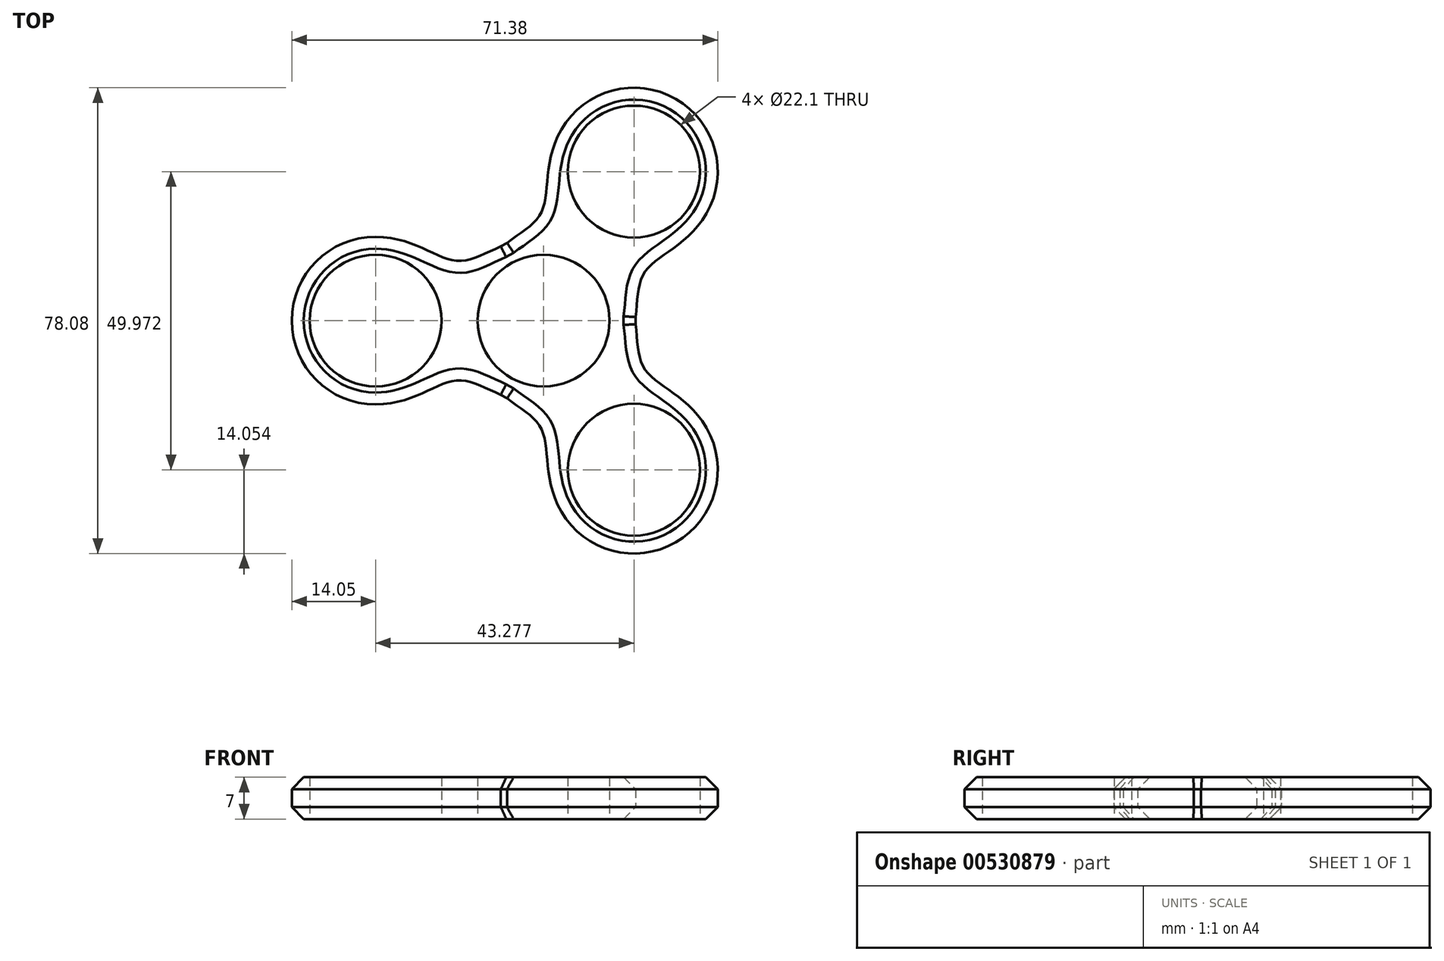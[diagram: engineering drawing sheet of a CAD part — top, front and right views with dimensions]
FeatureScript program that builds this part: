
annotation { "Feature Type Name" : "Feature", "Feature Type Description" : "" }
export const myFeature = defineFeature(function(context is Context, id is Id, definition is map)
    precondition{}
    {
        {
            var Q0;
            Q0=qCreatedBy(makeId("Top.planeOp"),FACE);
            var sketch = newSketch(context, id + "F0", { "sketchPlane" : qUnion([Q0])});
            skCircle(sketch, "E0", {"center": v(0, 0) * mm, "radius": 11 * mm, "construction": true});
            skCircle(sketch, "E1.0", {"center": v(0, 0) * mm, "radius": 11.05 * mm});
            skLineSegment(sketch, "E2", {"start": v(-11.05, 0) * mm, "end": v(-28.15, 0) * mm, "construction": true});
            skCircle(sketch, "E3", {"center": v(-28.15, 0) * mm, "radius": 11 * mm, "construction": true});
            skCircle(sketch, "E4.0", {"center": v(-28.15, 0) * mm, "radius": 11.05 * mm});
            skCircle(sketch, "E5.0", {"center": v(0, 0) * mm, "radius": 14.05 * mm});
            skCircle(sketch, "E6.0", {"center": v(-28.15, 0) * mm, "radius": 14.05 * mm});
            skLineSegment(sketch, "E7", {"start": v(-11.05, 0) * mm, "end": v(-17.1, 0) * mm, "construction": true});
            skLineSegment(sketch, "E8", {"start": v(-14.08, 10) * mm, "end": v(-14.08, -10) * mm, "construction": true});
            skPoint(sketch, "E9", {"position": v(-14.08, 0) * mm});
            skLineSegment(sketch, "E10", {"start": v(-21.57, -10) * mm, "end": v(-6.58, -10) * mm, "construction": true});
            skPoint(sketch, "E11", {"position": v(-14.08, -10) * mm});
            skLineSegment(sketch, "E12.MirrorCS", {"start": v(-21.57, 10) * mm, "end": v(-6.58, 10) * mm, "construction": true});
            skLineSegment(sketch, "E13", {"start": v(-28.15, 0) * mm, "end": v(-28.15, -14.05) * mm, "construction": true});
            skLineSegment(sketch, "E14", {"start": v(0, 0) * mm, "end": v(0, -14.05) * mm, "construction": true});
            skLineSegment(sketch, "E15", {"start": v(-21.57, -10) * mm, "end": v(-21.57, -14.05) * mm, "construction": true});
            skLineSegment(sketch, "E16", {"start": v(-6.58, -10) * mm, "end": v(-6.58, -14.05) * mm, "construction": true});
            skFitSpline(sketch, "E17", {"points": [v(-28.15, -14.05) * mm, v(-14.08, -10) * mm, v(0, -14.05) * mm], "startDerivative": vector(39.45, 0) * mm, "endDerivative": vector(39.45, 0) * mm});
            skFitSpline(sketch, "E18.MirrorCS", {"points": [v(-28.15, 14.05) * mm, v(-14.08, 10) * mm, v(0, 14.05) * mm], "startDerivative": vector(39.45, 0) * mm, "endDerivative": vector(39.45, 0) * mm});
            skLineSegment(sketch, "E19.MirrorCS", {"start": v(-21.57, 10) * mm, "end": v(-21.57, 14.05) * mm, "construction": true});
            skLineSegment(sketch, "E20.MirrorCS", {"start": v(-6.58, 10) * mm, "end": v(-6.58, 14.05) * mm, "construction": true});
            skLineSegment(sketch, "E21.1.0", {"start": v(1.05, -0.6) * mm, "end": v(13.22, 6.42) * mm, "construction": true});
            skLineSegment(sketch, "E21.1.1", {"start": v(13, -1.3) * mm, "end": v(16.5, 0.72) * mm, "construction": true});
            skLineSegment(sketch, "E21.1.2", {"start": v(20.5, -14.3) * mm, "end": v(13, -1.3) * mm, "construction": true});
            skLineSegment(sketch, "E21.1.3", {"start": v(20.5, -14.3) * mm, "end": v(24, -12.27) * mm, "construction": true});
            skCircle(sketch, "E21.1.4", {"center": v(15.13, -24.99) * mm, "radius": 11.05 * mm});
            skLineSegment(sketch, "E21.1.5", {"start": v(15.13, -24.99) * mm, "end": v(27.3, -17.96) * mm, "construction": true});
            skLineSegment(sketch, "E21.1.6", {"start": v(6.58, -10.18) * mm, "end": v(9.6, -15.42) * mm, "construction": true});
            skCircle(sketch, "E21.1.7", {"center": v(15.13, -24.99) * mm, "radius": 14.05 * mm});
            skLineSegment(sketch, "E21.2.0", {"start": v(1.05, 0.6) * mm, "end": v(-11.12, 7.63) * mm, "construction": true});
            skLineSegment(sketch, "E21.2.1", {"start": v(-4.32, 11.3) * mm, "end": v(-7.83, 13.33) * mm, "construction": true});
            skLineSegment(sketch, "E21.2.2", {"start": v(3.18, 24.3) * mm, "end": v(-4.32, 11.3) * mm, "construction": true});
            skLineSegment(sketch, "E21.2.3", {"start": v(3.18, 24.3) * mm, "end": v(-0.33, 26.32) * mm, "construction": true});
            skCircle(sketch, "E21.2.4", {"center": v(15.13, 24.99) * mm, "radius": 11.05 * mm});
            skLineSegment(sketch, "E21.2.5", {"start": v(15.13, 24.99) * mm, "end": v(2.96, 32.01) * mm, "construction": true});
            skLineSegment(sketch, "E21.2.6", {"start": v(6.58, 10.18) * mm, "end": v(9.6, 15.42) * mm, "construction": true});
            skCircle(sketch, "E21.2.7", {"center": v(15.13, 24.99) * mm, "radius": 14.05 * mm});
            skPoint(sketch, "E21.center", {"position": v(0.7, 0) * mm});
            skFitSpline(sketch, "E22", {"points": [v(-11.12, 7.63) * mm, v(-0.57, 17.8) * mm, v(2.96, 32.01) * mm], "startDerivative": vector(19.73, 34.16) * mm, "endDerivative": vector(19.72, 34.16) * mm});
            skFitSpline(sketch, "E23.MirrorCS", {"points": [v(13.22, -6.42) * mm, v(16.75, 7.8) * mm, v(27.3, 17.96) * mm], "startDerivative": vector(19.72, 34.16) * mm, "endDerivative": vector(19.73, 34.16) * mm});
            skFitSpline(sketch, "E24", {"points": [v(13.22, 6.42) * mm, v(16.75, -7.8) * mm, v(27.3, -17.96) * mm], "startDerivative": vector(19.72, -34.16) * mm, "endDerivative": vector(19.73, -34.16) * mm});
            skFitSpline(sketch, "E25.MirrorCS", {"points": [v(-11.12, -7.63) * mm, v(-0.57, -17.8) * mm, v(2.96, -32.01) * mm], "startDerivative": vector(19.73, -34.16) * mm, "endDerivative": vector(19.72, -34.16) * mm});
            skSolve(sketch);
        }
        {
            var Q0;
            {var subQ3=sQuery(id+"F0.wireOp",EDGE,"E22");var subQ9=sQuery(id+"F0.wireOp",EDGE,"E5.0");var subQ10=makeQuery(id+"F0.imprint","INTERSECT",VERTEX,{"derivedFrom":[subQ9,subQ3]});Q0=makeQuery(id+"F0.imprint","IMPRINT",FACE,{"disambiguationData":[TD([[makeQuery(id+"F0.imprint","IMPRINT",EDGE,{"disambiguationData":[TD([[subQ10,-1.0]])],"derivedFrom":subQ9}),-1.0]])]});}
            var Q1;
            Q1=makeQuery(id+"F0.imprint","IMPRINT",FACE,{"disambiguationData":[TD([[makeQuery(id+"F0.imprint","IMPRINT",EDGE,{"derivedFrom":sQuery(id+"F0.wireOp",EDGE,"E1.0")}),-1.0]])]});
            var Q2;
            Q2=makeQuery(id+"F0.imprint","IMPRINT",FACE,{"disambiguationData":[TD([[makeQuery(id+"F0.imprint","IMPRINT",EDGE,{"derivedFrom":sQuery(id+"F0.wireOp",EDGE,"E4.0")}),-1.0]])]});
            var Q3;
            {var subQ1=sQuery(id+"F0.wireOp",EDGE,"E5.0");var subQ5=sQuery(id+"F0.wireOp",EDGE,"E17");var subQ6=makeQuery(id+"F0.imprint","INTERSECT",VERTEX,{"derivedFrom":[subQ1,subQ5]});Q3=makeQuery(id+"F0.imprint","IMPRINT",FACE,{"disambiguationData":[TD([[makeQuery(id+"F0.imprint","IMPRINT",EDGE,{"disambiguationData":[TD([[subQ6,-1.0]])],"derivedFrom":subQ1}),-1.0]])]});}
            var Q4;
            Q4=makeQuery(id+"F0.imprint","IMPRINT",FACE,{"disambiguationData":[TD([[makeQuery(id+"F0.imprint","IMPRINT",EDGE,{"derivedFrom":sQuery(id+"F0.wireOp",EDGE,"E21.1.4")}),-1.0]])]});
            var Q5;
            {var subQ3=sQuery(id+"F0.wireOp",EDGE,"E18.MirrorCS");var subQ7=sQuery(id+"F0.wireOp",EDGE,"E5.0");var subQ8=makeQuery(id+"F0.imprint","INTERSECT",VERTEX,{"derivedFrom":[subQ7,subQ3]});Q5=makeQuery(id+"F0.imprint","IMPRINT",FACE,{"disambiguationData":[TD([[makeQuery(id+"F0.imprint","IMPRINT",EDGE,{"disambiguationData":[TD([[subQ8,1.0]])],"derivedFrom":subQ7}),-1.0]])]});}
            var Q6;
            Q6=makeQuery(id+"F0.imprint","IMPRINT",FACE,{"disambiguationData":[TD([[makeQuery(id+"F0.imprint","IMPRINT",EDGE,{"derivedFrom":sQuery(id+"F0.wireOp",EDGE,"E21.2.4")}),-1.0]])]});
            var Q7;
            {var subQ0=sQuery(id+"F0.wireOp",EDGE,"E18.MirrorCS");var subQ1=sQuery(id+"F0.wireOp",EDGE,"E5.0");var subQ2=makeQuery(id+"F0.imprint","INTERSECT",VERTEX,{"derivedFrom":[subQ1,subQ0]});Q7=makeQuery(id+"F0.imprint","IMPRINT",FACE,{"disambiguationData":[TD([[makeQuery(id+"F0.imprint","IMPRINT",EDGE,{"disambiguationData":[TD([[subQ2,-1.0]])],"derivedFrom":subQ1}),-1.0]])]});}
            var Q8;
            {var subQ0=sQuery(id+"F0.wireOp",EDGE,"E17");var subQ1=sQuery(id+"F0.wireOp",EDGE,"E5.0");var subQ2=makeQuery(id+"F0.imprint","INTERSECT",VERTEX,{"derivedFrom":[subQ1,subQ0]});Q8=makeQuery(id+"F0.imprint","IMPRINT",FACE,{"disambiguationData":[TD([[makeQuery(id+"F0.imprint","IMPRINT",EDGE,{"disambiguationData":[TD([[subQ2,1.0]])],"derivedFrom":subQ1}),-1.0]])]});}
            var Q9;
            {var subQ0=sQuery(id+"F0.wireOp",EDGE,"E23.MirrorCS");var subQ1=sQuery(id+"F0.wireOp",EDGE,"E5.0");var subQ2=makeQuery(id+"F0.imprint","INTERSECT",VERTEX,{"derivedFrom":[subQ1,subQ0]});Q9=makeQuery(id+"F0.imprint","IMPRINT",FACE,{"disambiguationData":[TD([[makeQuery(id+"F0.imprint","IMPRINT",EDGE,{"disambiguationData":[TD([[subQ2,-1.0]])],"derivedFrom":subQ1}),-1.0]])]});}
            extrude(context, id + "F1", {"entities" : qUnion([Q0, Q1, Q2, Q3, Q4, Q5, Q6, Q7, Q8, Q9]), "depth" : 7 * mm, "offsetDistance" : 25 * mm});
        }
        {
            var Q0;
            Q0=makeQuery(id+"F1.opExtrude","SWEPT_EDGE",EDGE,{"disambiguationData":[OSD([sQuery(id+"F0.wireOp",EDGE,"E17"),sQuery(id+"F0.wireOp",EDGE,"E25.MirrorCS")])]});
            var Q1;
            Q1=makeQuery(id+"F1.opExtrude","SWEPT_EDGE",EDGE,{"disambiguationData":[OSD([sQuery(id+"F0.wireOp",EDGE,"E23.MirrorCS"),sQuery(id+"F0.wireOp",EDGE,"E24")])]});
            var Q2;
            Q2=makeQuery(id+"F1.opExtrude","SWEPT_EDGE",EDGE,{"disambiguationData":[OSD([sQuery(id+"F0.wireOp",EDGE,"E18.MirrorCS"),sQuery(id+"F0.wireOp",EDGE,"E22")])]});
            chamfer(context, id + "F2", {"entities" : qUnion([Q0, Q1, Q2]), "width" : 5 * mm, "tangentPropagation" : true});
        }
        {
            var Q0;
            Q0=makeQuery(id+"F1.opExtrude","CAP_EDGE",EDGE,{"disambiguationData":[OSD([sQuery(id+"F0.wireOp",EDGE,"E21.1.7")])],"isStart":false});
            var Q1;
            Q1=makeQuery(id+"F1.opExtrude","CAP_EDGE",EDGE,{"disambiguationData":[OSD([sQuery(id+"F0.wireOp",EDGE,"E21.2.7")])],"isStart":true});
            var Q2;
            Q2=makeQuery(id+"F1.opExtrude","CAP_EDGE",EDGE,{"disambiguationData":[OSD([sQuery(id+"F0.wireOp",EDGE,"E6.0")])],"isStart":true});
            var Q3;
            Q3=makeQuery(id+"F1.opExtrude","CAP_EDGE",EDGE,{"disambiguationData":[OSD([sQuery(id+"F0.wireOp",EDGE,"E21.1.7")])],"isStart":true});
            var Q4;
            {var subQ0=sQuery(id+"F0.wireOp",EDGE,"E24");var subQ1=sQuery(id+"F0.wireOp",EDGE,"E23.MirrorCS");Q4=makeQuery(id+"F2.opChamfer","BLEND_EDGE",EDGE,{"blendedFrom":[makeQuery(id+"F1.opExtrude","SWEPT_EDGE",EDGE,{"disambiguationData":[OSD([subQ1,subQ0])]}),makeQuery(id+"F1.opExtrude","CAP_FACE",FACE,{"disambiguationData":[OSD([sQuery(id+"F0.wireOp",EDGE,"E1.0"),sQuery(id+"F0.wireOp",EDGE,"E4.0"),sQuery(id+"F0.wireOp",EDGE,"E6.0"),sQuery(id+"F0.wireOp",EDGE,"E17"),sQuery(id+"F0.wireOp",EDGE,"E18.MirrorCS"),sQuery(id+"F0.wireOp",EDGE,"E21.1.4"),sQuery(id+"F0.wireOp",EDGE,"E21.1.7"),sQuery(id+"F0.wireOp",EDGE,"E21.2.4"),sQuery(id+"F0.wireOp",EDGE,"E21.2.7"),sQuery(id+"F0.wireOp",EDGE,"E22"),subQ1,subQ0,sQuery(id+"F0.wireOp",EDGE,"E25.MirrorCS")])],"isStart":false})],"blendedInto":[makeQuery(id+"F1.opExtrude","CAP_FACE",FACE,{"disambiguationData":[OSD([sQuery(id+"F0.wireOp",EDGE,"E1.0"),sQuery(id+"F0.wireOp",EDGE,"E4.0"),sQuery(id+"F0.wireOp",EDGE,"E6.0"),sQuery(id+"F0.wireOp",EDGE,"E17"),sQuery(id+"F0.wireOp",EDGE,"E18.MirrorCS"),sQuery(id+"F0.wireOp",EDGE,"E21.1.4"),sQuery(id+"F0.wireOp",EDGE,"E21.1.7"),sQuery(id+"F0.wireOp",EDGE,"E21.2.4"),sQuery(id+"F0.wireOp",EDGE,"E21.2.7"),sQuery(id+"F0.wireOp",EDGE,"E22"),subQ1,subQ0,sQuery(id+"F0.wireOp",EDGE,"E25.MirrorCS")])],"isStart":false})]});}
            var Q5;
            Q5=makeQuery(id+"F1.opExtrude","SWEPT_FACE",FACE,{"disambiguationData":[OSD([sQuery(id+"F0.wireOp",EDGE,"E6.0")])]});
            var Q6;
            {var subQ0=sQuery(id+"F0.wireOp",EDGE,"E22");var subQ1=sQuery(id+"F0.wireOp",EDGE,"E18.MirrorCS");Q6=makeQuery(id+"F2.opChamfer","BLEND_EDGE",EDGE,{"blendedFrom":[makeQuery(id+"F1.opExtrude","SWEPT_EDGE",EDGE,{"disambiguationData":[OSD([subQ1,subQ0])]}),makeQuery(id+"F1.opExtrude","CAP_FACE",FACE,{"disambiguationData":[OSD([sQuery(id+"F0.wireOp",EDGE,"E1.0"),sQuery(id+"F0.wireOp",EDGE,"E4.0"),sQuery(id+"F0.wireOp",EDGE,"E6.0"),sQuery(id+"F0.wireOp",EDGE,"E17"),subQ1,sQuery(id+"F0.wireOp",EDGE,"E21.1.4"),sQuery(id+"F0.wireOp",EDGE,"E21.1.7"),sQuery(id+"F0.wireOp",EDGE,"E21.2.4"),sQuery(id+"F0.wireOp",EDGE,"E21.2.7"),subQ0,sQuery(id+"F0.wireOp",EDGE,"E23.MirrorCS"),sQuery(id+"F0.wireOp",EDGE,"E24"),sQuery(id+"F0.wireOp",EDGE,"E25.MirrorCS")])],"isStart":false})],"blendedInto":[makeQuery(id+"F1.opExtrude","CAP_FACE",FACE,{"disambiguationData":[OSD([sQuery(id+"F0.wireOp",EDGE,"E1.0"),sQuery(id+"F0.wireOp",EDGE,"E4.0"),sQuery(id+"F0.wireOp",EDGE,"E6.0"),sQuery(id+"F0.wireOp",EDGE,"E17"),subQ1,sQuery(id+"F0.wireOp",EDGE,"E21.1.4"),sQuery(id+"F0.wireOp",EDGE,"E21.1.7"),sQuery(id+"F0.wireOp",EDGE,"E21.2.4"),sQuery(id+"F0.wireOp",EDGE,"E21.2.7"),subQ0,sQuery(id+"F0.wireOp",EDGE,"E23.MirrorCS"),sQuery(id+"F0.wireOp",EDGE,"E24"),sQuery(id+"F0.wireOp",EDGE,"E25.MirrorCS")])],"isStart":false})]});}
            var Q7;
            Q7=makeQuery(id+"F1.opExtrude","CAP_EDGE",EDGE,{"disambiguationData":[OSD([sQuery(id+"F0.wireOp",EDGE,"E21.2.7")])],"isStart":false});
            var Q8;
            {var subQ0=sQuery(id+"F0.wireOp",EDGE,"E25.MirrorCS");var subQ1=sQuery(id+"F0.wireOp",EDGE,"E17");Q8=makeQuery(id+"F2.opChamfer","BLEND_EDGE",EDGE,{"blendedFrom":[makeQuery(id+"F1.opExtrude","SWEPT_EDGE",EDGE,{"disambiguationData":[OSD([subQ1,subQ0])]}),makeQuery(id+"F1.opExtrude","CAP_FACE",FACE,{"disambiguationData":[OSD([sQuery(id+"F0.wireOp",EDGE,"E1.0"),sQuery(id+"F0.wireOp",EDGE,"E4.0"),sQuery(id+"F0.wireOp",EDGE,"E6.0"),subQ1,sQuery(id+"F0.wireOp",EDGE,"E18.MirrorCS"),sQuery(id+"F0.wireOp",EDGE,"E21.1.4"),sQuery(id+"F0.wireOp",EDGE,"E21.1.7"),sQuery(id+"F0.wireOp",EDGE,"E21.2.4"),sQuery(id+"F0.wireOp",EDGE,"E21.2.7"),sQuery(id+"F0.wireOp",EDGE,"E22"),sQuery(id+"F0.wireOp",EDGE,"E23.MirrorCS"),sQuery(id+"F0.wireOp",EDGE,"E24"),subQ0])],"isStart":false})],"blendedInto":[makeQuery(id+"F1.opExtrude","CAP_FACE",FACE,{"disambiguationData":[OSD([sQuery(id+"F0.wireOp",EDGE,"E1.0"),sQuery(id+"F0.wireOp",EDGE,"E4.0"),sQuery(id+"F0.wireOp",EDGE,"E6.0"),subQ1,sQuery(id+"F0.wireOp",EDGE,"E18.MirrorCS"),sQuery(id+"F0.wireOp",EDGE,"E21.1.4"),sQuery(id+"F0.wireOp",EDGE,"E21.1.7"),sQuery(id+"F0.wireOp",EDGE,"E21.2.4"),sQuery(id+"F0.wireOp",EDGE,"E21.2.7"),sQuery(id+"F0.wireOp",EDGE,"E22"),sQuery(id+"F0.wireOp",EDGE,"E23.MirrorCS"),sQuery(id+"F0.wireOp",EDGE,"E24"),subQ0])],"isStart":false})]});}
            var Q9;
            {var subQ0=sQuery(id+"F0.wireOp",EDGE,"E25.MirrorCS");var subQ1=sQuery(id+"F0.wireOp",EDGE,"E17");Q9=makeQuery(id+"F2.opChamfer","BLEND_EDGE",EDGE,{"blendedFrom":[makeQuery(id+"F1.opExtrude","SWEPT_EDGE",EDGE,{"disambiguationData":[OSD([subQ1,subQ0])]}),makeQuery(id+"F1.opExtrude","CAP_FACE",FACE,{"disambiguationData":[OSD([sQuery(id+"F0.wireOp",EDGE,"E1.0"),sQuery(id+"F0.wireOp",EDGE,"E4.0"),sQuery(id+"F0.wireOp",EDGE,"E6.0"),subQ1,sQuery(id+"F0.wireOp",EDGE,"E18.MirrorCS"),sQuery(id+"F0.wireOp",EDGE,"E21.1.4"),sQuery(id+"F0.wireOp",EDGE,"E21.1.7"),sQuery(id+"F0.wireOp",EDGE,"E21.2.4"),sQuery(id+"F0.wireOp",EDGE,"E21.2.7"),sQuery(id+"F0.wireOp",EDGE,"E22"),sQuery(id+"F0.wireOp",EDGE,"E23.MirrorCS"),sQuery(id+"F0.wireOp",EDGE,"E24"),subQ0])],"isStart":true})],"blendedInto":[makeQuery(id+"F1.opExtrude","CAP_FACE",FACE,{"disambiguationData":[OSD([sQuery(id+"F0.wireOp",EDGE,"E1.0"),sQuery(id+"F0.wireOp",EDGE,"E4.0"),sQuery(id+"F0.wireOp",EDGE,"E6.0"),subQ1,sQuery(id+"F0.wireOp",EDGE,"E18.MirrorCS"),sQuery(id+"F0.wireOp",EDGE,"E21.1.4"),sQuery(id+"F0.wireOp",EDGE,"E21.1.7"),sQuery(id+"F0.wireOp",EDGE,"E21.2.4"),sQuery(id+"F0.wireOp",EDGE,"E21.2.7"),sQuery(id+"F0.wireOp",EDGE,"E22"),sQuery(id+"F0.wireOp",EDGE,"E23.MirrorCS"),sQuery(id+"F0.wireOp",EDGE,"E24"),subQ0])],"isStart":true})]});}
            var Q10;
            {var subQ0=sQuery(id+"F0.wireOp",EDGE,"E24");var subQ1=sQuery(id+"F0.wireOp",EDGE,"E23.MirrorCS");Q10=makeQuery(id+"F2.opChamfer","BLEND_EDGE",EDGE,{"blendedFrom":[makeQuery(id+"F1.opExtrude","SWEPT_EDGE",EDGE,{"disambiguationData":[OSD([subQ1,subQ0])]}),makeQuery(id+"F1.opExtrude","CAP_FACE",FACE,{"disambiguationData":[OSD([sQuery(id+"F0.wireOp",EDGE,"E1.0"),sQuery(id+"F0.wireOp",EDGE,"E4.0"),sQuery(id+"F0.wireOp",EDGE,"E6.0"),sQuery(id+"F0.wireOp",EDGE,"E17"),sQuery(id+"F0.wireOp",EDGE,"E18.MirrorCS"),sQuery(id+"F0.wireOp",EDGE,"E21.1.4"),sQuery(id+"F0.wireOp",EDGE,"E21.1.7"),sQuery(id+"F0.wireOp",EDGE,"E21.2.4"),sQuery(id+"F0.wireOp",EDGE,"E21.2.7"),sQuery(id+"F0.wireOp",EDGE,"E22"),subQ1,subQ0,sQuery(id+"F0.wireOp",EDGE,"E25.MirrorCS")])],"isStart":true})],"blendedInto":[makeQuery(id+"F1.opExtrude","CAP_FACE",FACE,{"disambiguationData":[OSD([sQuery(id+"F0.wireOp",EDGE,"E1.0"),sQuery(id+"F0.wireOp",EDGE,"E4.0"),sQuery(id+"F0.wireOp",EDGE,"E6.0"),sQuery(id+"F0.wireOp",EDGE,"E17"),sQuery(id+"F0.wireOp",EDGE,"E18.MirrorCS"),sQuery(id+"F0.wireOp",EDGE,"E21.1.4"),sQuery(id+"F0.wireOp",EDGE,"E21.1.7"),sQuery(id+"F0.wireOp",EDGE,"E21.2.4"),sQuery(id+"F0.wireOp",EDGE,"E21.2.7"),sQuery(id+"F0.wireOp",EDGE,"E22"),subQ1,subQ0,sQuery(id+"F0.wireOp",EDGE,"E25.MirrorCS")])],"isStart":true})]});}
            var Q11;
            {var subQ0=sQuery(id+"F0.wireOp",EDGE,"E22");var subQ1=sQuery(id+"F0.wireOp",EDGE,"E18.MirrorCS");Q11=makeQuery(id+"F2.opChamfer","BLEND_EDGE",EDGE,{"blendedFrom":[makeQuery(id+"F1.opExtrude","SWEPT_EDGE",EDGE,{"disambiguationData":[OSD([subQ1,subQ0])]}),makeQuery(id+"F1.opExtrude","CAP_FACE",FACE,{"disambiguationData":[OSD([sQuery(id+"F0.wireOp",EDGE,"E1.0"),sQuery(id+"F0.wireOp",EDGE,"E4.0"),sQuery(id+"F0.wireOp",EDGE,"E6.0"),sQuery(id+"F0.wireOp",EDGE,"E17"),subQ1,sQuery(id+"F0.wireOp",EDGE,"E21.1.4"),sQuery(id+"F0.wireOp",EDGE,"E21.1.7"),sQuery(id+"F0.wireOp",EDGE,"E21.2.4"),sQuery(id+"F0.wireOp",EDGE,"E21.2.7"),subQ0,sQuery(id+"F0.wireOp",EDGE,"E23.MirrorCS"),sQuery(id+"F0.wireOp",EDGE,"E24"),sQuery(id+"F0.wireOp",EDGE,"E25.MirrorCS")])],"isStart":true})],"blendedInto":[makeQuery(id+"F1.opExtrude","CAP_FACE",FACE,{"disambiguationData":[OSD([sQuery(id+"F0.wireOp",EDGE,"E1.0"),sQuery(id+"F0.wireOp",EDGE,"E4.0"),sQuery(id+"F0.wireOp",EDGE,"E6.0"),sQuery(id+"F0.wireOp",EDGE,"E17"),subQ1,sQuery(id+"F0.wireOp",EDGE,"E21.1.4"),sQuery(id+"F0.wireOp",EDGE,"E21.1.7"),sQuery(id+"F0.wireOp",EDGE,"E21.2.4"),sQuery(id+"F0.wireOp",EDGE,"E21.2.7"),subQ0,sQuery(id+"F0.wireOp",EDGE,"E23.MirrorCS"),sQuery(id+"F0.wireOp",EDGE,"E24"),sQuery(id+"F0.wireOp",EDGE,"E25.MirrorCS")])],"isStart":true})]});}
            chamfer(context, id + "F3", {"entities" : qUnion([Q0, Q1, Q2, Q3, Q4, Q5, Q6, Q7, Q8, Q9, Q10, Q11]), "width" : 2 * mm, "tangentPropagation" : true});
        }
    });
